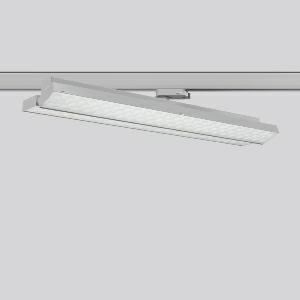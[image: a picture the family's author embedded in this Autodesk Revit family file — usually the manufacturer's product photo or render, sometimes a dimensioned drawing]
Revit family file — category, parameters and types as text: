
# Revit family: tx-move_742161_004_2_6fe4
name_source: partatom
category: Lighting Fixtures
units: mm (PartAtom-declared; Revit-internal decimal feet)

## family parameters
Cut with Voids When Loaded = No
Host = Face
Light Source = No
Part Type = Normal
Room Calculation Point = No
Round Connector Dimension = Use Diameter
Shared = No

## types (1)
- MultiLumen 1 (1 x LED Modul 927, 2125 lm, 2700)
    Apparent Load = 38 VA
    CIE Flux Codes = 90 97 99 100 100
    Color Rendering = 92
    Color Temperature = 2700
    Default Elevation = 1800 mm
    Description = Series: TX-MOVE
Multifunctional surface-mounted spotlight for area lighting. Very flat design. Housing: sheet steel, powder-coated. Rotation range: 356°. Swivel range: 90°. Consistent alignment possible with visible tilt scale. High-efficiency LED units with optimum light control thanks to clear plastic (PC) lens optics. Spezielle Mikrostrukturen reduzieren Gelbsaum. Symmetrical light distribution. Best colour rendering with CRI >90 for fresh products and coloured textiles. With multi adaptor for 3-circuit tracks 230 V. Suitable for Track on ceiling. MultiLumen: Luminous flux adjustable in 3 steps. Factory setting is the highest luminous flux. Environmentally friendly and resource-saving due to replaceable and recyclable components. Very good glare control, ideal for till areas. 
Colour: silver, matt (approx. RAL 9006)
Length: 570 mm
Width: 119 mm
Height: 92 mm
Lamp: LED
Socket: without socket
Colour temperature: 2700K
Colour rendering index (CRI): 90
System power: 38 W
Rated luminous flux: 4250 lm
Luminous efficiency: 112 lm/W
System power 2: 51 W
Rated luminous flux 2: 5550 lm
Luminous efficiency 2: 109 lm/W
System power 3: 62 W
Rated luminous flux 3: 6600 lm
Luminous efficiency 3: 106 lm/W
Control gear: Regulated power supply
Protection class: I
Type of protection: IP 20
    Height = 75 mm
    Lamp = 1 x LED Modul 927
    Lamp Light Flux = 2125 lm
    Lamp count = 1
    Length = 569 mm
    Lifetime = 50000 h
    Luminous efficacy = 112 lm/W
    Manufacturer = RZB
    ModVariant = No
    Model = 742161.004.2
    Mounting Place = Ceiling
    Mounting Type = Surface mounted
    Number of Poles = 1
    OnlyDefault = Yes
    Power Factor = 1
    Product Name = TX-MOVE
    Product group = Track mounted projectors
    ProductGroupID = 301
    Protection Class = Protection class I
    Protection Degree = IP 20
    RLX_Detail_Level = 1
    RLX_Emergency_Light_Flux = 0 lm
    RLX_Emergency_Type = 0
    RLX_Emergency_Type_DB = No
    RlxData = <blob elided: 33329 chars, md5=0c863846>
    Socket = socket
    Standby Power = 0 W
    System Light Flux = 4250 lm
    System Power = 38 W
    Type Comments = MultiLumen 1
    Type Image = 742162.004.jpg
    URL = http://relux.com
    VarID = multilumen_1
    Voltage = 0 V
    Weight = 0.00 kg
    Width = 119 mm

## geometry (parser evidence)
native form markers: Blend x4, Sweep x16
no freeform markers — native parametric forms only
